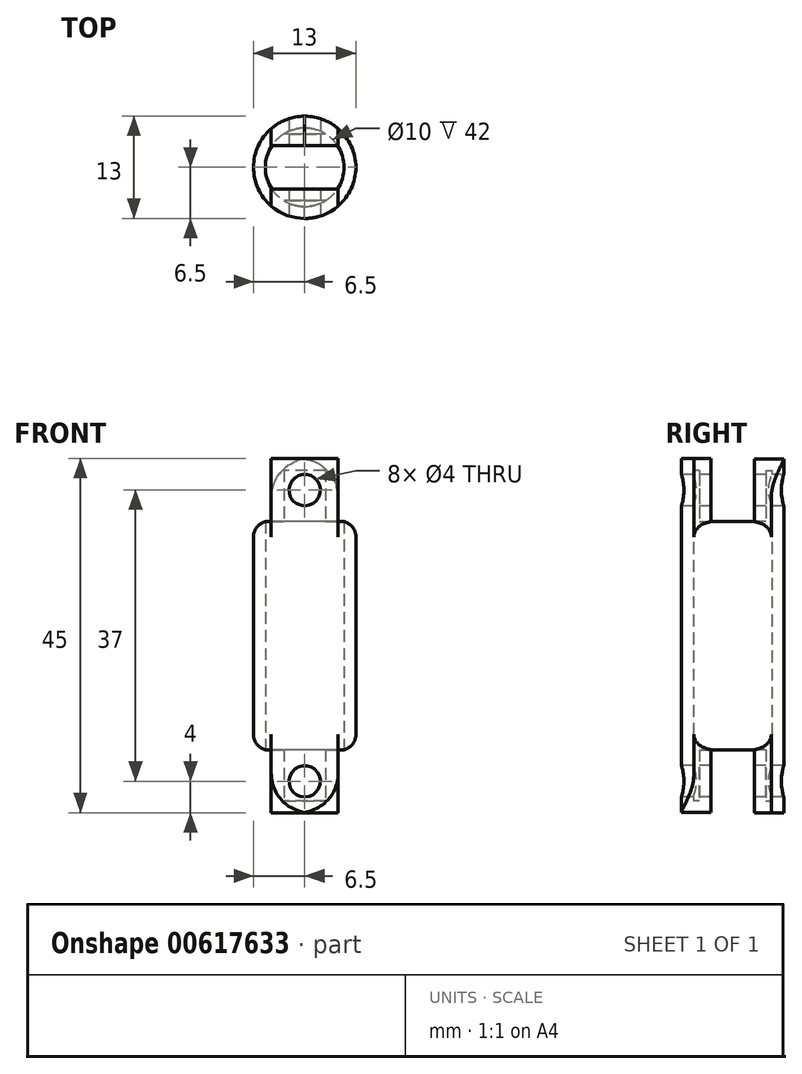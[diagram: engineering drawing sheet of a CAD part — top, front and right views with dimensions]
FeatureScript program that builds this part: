
annotation { "Feature Type Name" : "Feature", "Feature Type Description" : "" }
export const myFeature = defineFeature(function(context is Context, id is Id, definition is map)
    precondition{}
    {
        {
            var Q0;
            Q0=qCreatedBy(makeId("Top.planeOp"),FACE);
            var sketch = newSketch(context, id + "F0", { "sketchPlane" : qUnion([Q0])});
            skCircle(sketch, "E0", {"center": v(0, 0) * mm, "radius": 6.5 * mm});
            skSolve(sketch);
        }
        {
            var Q0;
            Q0 = qSketchRegion(id + "F0", true);
            extrude(context, id + "F1", {"entities" : qUnion([Q0]), "depth" : 45 * mm, "offsetDistance" : 25 * mm});
        }
        {
            var Q0;
            Q0=makeQuery(id+"F1.opExtrude","CAP_FACE",FACE,{"disambiguationData":[OSD([sQuery(id+"F0.wireOp",EDGE,"E0")])],"isStart":true});
            var sketch = newSketch(context, id + "F2", { "sketchPlane" : qUnion([Q0])});
            skLineSegment(sketch, "E1.bottom", {"start": v(6, 2.75) * mm, "end": v(-6, 2.75) * mm});
            skLineSegment(sketch, "E1.top", {"start": v(6, -2.75) * mm, "end": v(-6, -2.75) * mm});
            skLineSegment(sketch, "E1.left", {"start": v(6, 2.75) * mm, "end": v(6, -2.75) * mm});
            skLineSegment(sketch, "E1.right", {"start": v(-6, 2.75) * mm, "end": v(-6, -2.75) * mm});
            skPoint(sketch, "E1.middle", {"position": v(0, 0) * mm});
            skLineSegment(sketch, "E2.bottom", {"start": v(-4.25, 5) * mm, "end": v(-7.75, 5) * mm});
            skLineSegment(sketch, "E2.top", {"start": v(-4.25, -5) * mm, "end": v(-7.75, -5) * mm});
            skLineSegment(sketch, "E2.left", {"start": v(-4.25, 5) * mm, "end": v(-4.25, -5) * mm});
            skLineSegment(sketch, "E2.right", {"start": v(-7.75, 5) * mm, "end": v(-7.75, -5) * mm});
            skPoint(sketch, "E2.middle", {"position": v(-6, 0) * mm});
            skLineSegment(sketch, "E3.bottom", {"start": v(7.75, 5) * mm, "end": v(4.25, 5) * mm});
            skLineSegment(sketch, "E3.top", {"start": v(7.75, -5) * mm, "end": v(4.25, -5) * mm});
            skLineSegment(sketch, "E3.left", {"start": v(7.75, 5) * mm, "end": v(7.75, -5) * mm});
            skLineSegment(sketch, "E3.right", {"start": v(4.25, 5) * mm, "end": v(4.25, -5) * mm});
            skPoint(sketch, "E3.middle", {"position": v(6, 0) * mm});
            skSolve(sketch);
        }
        {
            var Q0;
            Q0 = qSketchRegion(id + "F2", true);
            extrude(context, id + "F3", {"entities" : qUnion([Q0]), "operationType" : NewBodyOperationType.REMOVE, "oppositeDirection" : true, "depth" : 8 * mm, "offsetDistance" : 25 * mm});
        }
        {
            var Q0;
            Q0=makeQuery(id+"F1.opExtrude","CAP_FACE",FACE,{"disambiguationData":[OSD([sQuery(id+"F0.wireOp",EDGE,"E0")])],"isStart":false});
            var sketch = newSketch(context, id + "F4", { "sketchPlane" : qUnion([Q0])});
            skLineSegment(sketch, "E4.bottom", {"start": v(6, 2.75) * mm, "end": v(-6, 2.75) * mm});
            skLineSegment(sketch, "E4.top", {"start": v(6, -2.75) * mm, "end": v(-6, -2.75) * mm});
            skLineSegment(sketch, "E4.left", {"start": v(6, 2.75) * mm, "end": v(6, -2.75) * mm});
            skLineSegment(sketch, "E4.right", {"start": v(-6, 2.75) * mm, "end": v(-6, -2.75) * mm});
            skPoint(sketch, "E4.middle", {"position": v(0, 0) * mm});
            skLineSegment(sketch, "E5.bottom", {"start": v(7.75, 5) * mm, "end": v(4.25, 5) * mm});
            skLineSegment(sketch, "E5.top", {"start": v(7.75, -5) * mm, "end": v(4.25, -5) * mm});
            skLineSegment(sketch, "E5.left", {"start": v(7.75, 5) * mm, "end": v(7.75, -5) * mm});
            skLineSegment(sketch, "E5.right", {"start": v(4.25, 5) * mm, "end": v(4.25, -5) * mm});
            skPoint(sketch, "E5.middle", {"position": v(6, 0) * mm});
            skLineSegment(sketch, "E6.bottom", {"start": v(-4.25, 5) * mm, "end": v(-7.75, 5) * mm});
            skLineSegment(sketch, "E6.top", {"start": v(-4.25, -5) * mm, "end": v(-7.75, -5) * mm});
            skLineSegment(sketch, "E6.left", {"start": v(-4.25, 5) * mm, "end": v(-4.25, -5) * mm});
            skLineSegment(sketch, "E6.right", {"start": v(-7.75, 5) * mm, "end": v(-7.75, -5) * mm});
            skPoint(sketch, "E6.middle", {"position": v(-6, 0) * mm});
            skSolve(sketch);
        }
        {
            var Q0;
            Q0 = qSketchRegion(id + "F4", true);
            extrude(context, id + "F5", {"entities" : qUnion([Q0]), "operationType" : NewBodyOperationType.REMOVE, "oppositeDirection" : true, "depth" : 8 * mm, "offsetDistance" : 25 * mm});
        }
        {
            var Q0;
            Q0=makeQuery(id+"F3.boolean.opBoolean","COPY",FACE,{"derivedFrom":makeQuery(id+"F3.opExtrude","SWEPT_FACE",FACE,{"disambiguationData":[OSD([sQuery(id+"F2.wireOp",EDGE,"E1.top")])]})});
            var sketch = newSketch(context, id + "F6", { "sketchPlane" : qUnion([Q0])});
            skCircle(sketch, "E7", {"center": v(0, 4) * mm, "radius": 2 * mm});
            skPoint(sketch, "E7.centerSnap0", {"position": v(-4.18, 4) * mm});
            skSolve(sketch);
        }
        {
            var Q0;
            Q0=makeQuery(id+"F3.boolean.opBoolean","COPY",FACE,{"derivedFrom":makeQuery(id+"F3.opExtrude","CAP_FACE",FACE,{"disambiguationData":[OSD([sQuery(id+"F2.wireOp",EDGE,"E1.bottom"),sQuery(id+"F2.wireOp",EDGE,"E1.top"),sQuery(id+"F2.wireOp",EDGE,"E2.bottom"),sQuery(id+"F2.wireOp",EDGE,"E2.top"),sQuery(id+"F2.wireOp",EDGE,"E2.left"),sQuery(id+"F2.wireOp",EDGE,"E2.right"),sQuery(id+"F2.wireOp",EDGE,"E3.bottom"),sQuery(id+"F2.wireOp",EDGE,"E3.top"),sQuery(id+"F2.wireOp",EDGE,"E3.left"),sQuery(id+"F2.wireOp",EDGE,"E3.right")])],"isStart":false})});
            var Q1;
            Q1=makeQuery(id+"F5.boolean.opBoolean","COPY",FACE,{"derivedFrom":makeQuery(id+"F5.opExtrude","CAP_FACE",FACE,{"disambiguationData":[OSD([sQuery(id+"F4.wireOp",EDGE,"E4.bottom"),sQuery(id+"F4.wireOp",EDGE,"E4.top"),sQuery(id+"F4.wireOp",EDGE,"E5.bottom"),sQuery(id+"F4.wireOp",EDGE,"E5.top"),sQuery(id+"F4.wireOp",EDGE,"E5.left"),sQuery(id+"F4.wireOp",EDGE,"E5.right"),sQuery(id+"F4.wireOp",EDGE,"E6.bottom"),sQuery(id+"F4.wireOp",EDGE,"E6.top"),sQuery(id+"F4.wireOp",EDGE,"E6.left"),sQuery(id+"F4.wireOp",EDGE,"E6.right")])],"isStart":false})});
            shell(context, id + "F7", {"entities" : qUnion([Q0, Q1]), "thickness" : 1.5 * mm});
        }
        {
            var Q0;
            Q0=makeQuery(id+"F5.boolean.opBoolean","COPY",FACE,{"derivedFrom":makeQuery(id+"F5.opExtrude","SWEPT_FACE",FACE,{"disambiguationData":[OSD([sQuery(id+"F4.wireOp",EDGE,"E4.bottom")])]})});
            var sketch = newSketch(context, id + "F8", { "sketchPlane" : qUnion([Q0])});
            skCircle(sketch, "E8", {"center": v(0, 41) * mm, "radius": 2 * mm});
            skPoint(sketch, "E8.centerSnap0", {"position": v(-4.25, 41) * mm});
            skPoint(sketch, "E9", {"position": v(6.83, 41) * mm});
            skSolve(sketch);
        }
        {
            var Q0;
            Q0 = qSketchRegion(id + "F8", true);
            extrude(context, id + "F9", {"entities" : qUnion([Q0]), "operationType" : NewBodyOperationType.REMOVE, "oppositeDirection" : true, "depth" : 25 * mm, "offsetDistance" : 25 * mm, "hasSecondDirection" : true, "secondDirectionOppositeDirection" : false, "secondDirectionDepth" : 25 * mm});
        }
        {
            var Q0;
            Q0 = qSketchRegion(id + "F6", true);
            extrude(context, id + "F10", {"entities" : qUnion([Q0]), "operationType" : NewBodyOperationType.REMOVE, "oppositeDirection" : true, "depth" : 25 * mm, "offsetDistance" : 25 * mm, "hasSecondDirection" : true, "secondDirectionOppositeDirection" : false, "secondDirectionDepth" : 25 * mm});
        }
        {
            var Q0;
            Q0=makeQuery(id+"F5.boolean.opBoolean","COPY",FACE,{"derivedFrom":makeQuery(id+"F5.opExtrude","SWEPT_FACE",FACE,{"disambiguationData":[OSD([sQuery(id+"F4.wireOp",EDGE,"E4.bottom")])]})});
            var sketch = newSketch(context, id + "F11", { "sketchPlane" : qUnion([Q0])});
            skCircle(sketch, "E10", {"center": v(0, 41) * mm, "radius": 5 * mm});
            skSolve(sketch);
        }
        {
            var Q0;
            Q0 = qSketchRegion(id + "F11", true);
            extrude(context, id + "F12", {"entities" : qUnion([Q0]), "operationType" : NewBodyOperationType.REMOVE, "depth" : 5.5 * mm, "offsetDistance" : 25 * mm});
        }
        {
            var Q0;
            Q0=makeQuery(id+"F3.boolean.opBoolean","COPY",FACE,{"derivedFrom":makeQuery(id+"F3.opExtrude","SWEPT_FACE",FACE,{"disambiguationData":[OSD([sQuery(id+"F2.wireOp",EDGE,"E1.top")])]})});
            var sketch = newSketch(context, id + "F13", { "sketchPlane" : qUnion([Q0])});
            skCircle(sketch, "E11", {"center": v(0, 4) * mm, "radius": 5 * mm});
            skSolve(sketch);
        }
        {
            var Q0;
            Q0 = qSketchRegion(id + "F13", true);
            extrude(context, id + "F14", {"entities" : qUnion([Q0]), "operationType" : NewBodyOperationType.REMOVE, "depth" : 5.5 * mm, "offsetDistance" : 25 * mm});
        }
        {
            var Q0;
            {var subQ0=sQuery(id+"F4.wireOp",EDGE,"E5.right");Q0=makeQuery(id+"F5.boolean.opBoolean","COPY",EDGE,{"derivedFrom":makeQuery(id+"F5.opExtrude","CAP_EDGE",EDGE,{"disambiguationData":[OSD([subQ0]),TDD([makeQuery(id+"F4.imprint","IMPRINT",EDGE,{"disambiguationData":[TD([[makeQuery(id+"F4.imprint","INTERSECT",VERTEX,{"derivedFrom":[sQuery(id+"F4.wireOp",EDGE,"E4.top"),subQ0]}),-1.0]])],"derivedFrom":subQ0}),makeQuery(id+"F4.imprint","IMPRINT",EDGE,{"disambiguationData":[TD([[makeQuery(id+"F4.imprint","INTERSECT",VERTEX,{"derivedFrom":[sQuery(id+"F4.wireOp",EDGE,"E5.top"),subQ0]}),1.0]])],"derivedFrom":subQ0})])],"isStart":true})});}
            var Q1;
            {var subQ0=sQuery(id+"F4.wireOp",EDGE,"E5.right");Q1=makeQuery(id+"F5.boolean.opBoolean","COPY",EDGE,{"derivedFrom":makeQuery(id+"F5.opExtrude","CAP_EDGE",EDGE,{"disambiguationData":[OSD([subQ0]),TDD([makeQuery(id+"F4.imprint","IMPRINT",EDGE,{"disambiguationData":[TD([[makeQuery(id+"F4.imprint","INTERSECT",VERTEX,{"derivedFrom":[sQuery(id+"F4.wireOp",EDGE,"E5.bottom"),subQ0]}),-1.0]])],"derivedFrom":subQ0}),makeQuery(id+"F4.imprint","IMPRINT",EDGE,{"disambiguationData":[TD([[makeQuery(id+"F4.imprint","INTERSECT",VERTEX,{"derivedFrom":[sQuery(id+"F4.wireOp",EDGE,"E4.bottom"),subQ0]}),1.0]])],"derivedFrom":subQ0})])],"isStart":true})});}
            var Q2;
            {var subQ0=sQuery(id+"F4.wireOp",EDGE,"E6.left");Q2=makeQuery(id+"F5.boolean.opBoolean","COPY",EDGE,{"derivedFrom":makeQuery(id+"F5.opExtrude","CAP_EDGE",EDGE,{"disambiguationData":[OSD([subQ0]),TDD([makeQuery(id+"F4.imprint","IMPRINT",EDGE,{"disambiguationData":[TD([[makeQuery(id+"F4.imprint","INTERSECT",VERTEX,{"derivedFrom":[sQuery(id+"F4.wireOp",EDGE,"E4.top"),subQ0]}),-1.0]])],"derivedFrom":subQ0}),makeQuery(id+"F4.imprint","IMPRINT",EDGE,{"disambiguationData":[TD([[makeQuery(id+"F4.imprint","INTERSECT",VERTEX,{"derivedFrom":[sQuery(id+"F4.wireOp",EDGE,"E6.top"),subQ0]}),1.0]])],"derivedFrom":subQ0})])],"isStart":true})});}
            var Q3;
            {var subQ0=sQuery(id+"F4.wireOp",EDGE,"E6.left");Q3=makeQuery(id+"F5.boolean.opBoolean","COPY",EDGE,{"derivedFrom":makeQuery(id+"F5.opExtrude","CAP_EDGE",EDGE,{"disambiguationData":[OSD([subQ0]),TDD([makeQuery(id+"F4.imprint","IMPRINT",EDGE,{"disambiguationData":[TD([[makeQuery(id+"F4.imprint","INTERSECT",VERTEX,{"derivedFrom":[sQuery(id+"F4.wireOp",EDGE,"E6.bottom"),subQ0]}),-1.0]])],"derivedFrom":subQ0}),makeQuery(id+"F4.imprint","IMPRINT",EDGE,{"disambiguationData":[TD([[makeQuery(id+"F4.imprint","INTERSECT",VERTEX,{"derivedFrom":[sQuery(id+"F4.wireOp",EDGE,"E4.bottom"),subQ0]}),1.0]])],"derivedFrom":subQ0})])],"isStart":true})});}
            var Q4;
            {var subQ0=sQuery(id+"F2.wireOp",EDGE,"E2.left");Q4=makeQuery(id+"F3.boolean.opBoolean","COPY",EDGE,{"derivedFrom":makeQuery(id+"F3.opExtrude","CAP_EDGE",EDGE,{"disambiguationData":[OSD([subQ0]),TDD([makeQuery(id+"F2.imprint","IMPRINT",EDGE,{"disambiguationData":[TD([[makeQuery(id+"F2.imprint","INTERSECT",VERTEX,{"derivedFrom":[sQuery(id+"F2.wireOp",EDGE,"E1.top"),subQ0]}),-1.0]])],"derivedFrom":subQ0}),makeQuery(id+"F2.imprint","IMPRINT",EDGE,{"disambiguationData":[TD([[makeQuery(id+"F2.imprint","INTERSECT",VERTEX,{"derivedFrom":[sQuery(id+"F2.wireOp",EDGE,"E2.top"),subQ0]}),1.0]])],"derivedFrom":subQ0})])],"isStart":true})});}
            var Q5;
            {var subQ0=sQuery(id+"F2.wireOp",EDGE,"E3.right");Q5=makeQuery(id+"F3.boolean.opBoolean","COPY",EDGE,{"derivedFrom":makeQuery(id+"F3.opExtrude","CAP_EDGE",EDGE,{"disambiguationData":[OSD([subQ0]),TDD([makeQuery(id+"F2.imprint","IMPRINT",EDGE,{"disambiguationData":[TD([[makeQuery(id+"F2.imprint","INTERSECT",VERTEX,{"derivedFrom":[sQuery(id+"F2.wireOp",EDGE,"E1.top"),subQ0]}),-1.0]])],"derivedFrom":subQ0}),makeQuery(id+"F2.imprint","IMPRINT",EDGE,{"disambiguationData":[TD([[makeQuery(id+"F2.imprint","INTERSECT",VERTEX,{"derivedFrom":[sQuery(id+"F2.wireOp",EDGE,"E3.top"),subQ0]}),1.0]])],"derivedFrom":subQ0})])],"isStart":true})});}
            var Q6;
            {var subQ0=sQuery(id+"F2.wireOp",EDGE,"E3.right");Q6=makeQuery(id+"F3.boolean.opBoolean","COPY",EDGE,{"derivedFrom":makeQuery(id+"F3.opExtrude","CAP_EDGE",EDGE,{"disambiguationData":[OSD([subQ0]),TDD([makeQuery(id+"F2.imprint","IMPRINT",EDGE,{"disambiguationData":[TD([[makeQuery(id+"F2.imprint","INTERSECT",VERTEX,{"derivedFrom":[sQuery(id+"F2.wireOp",EDGE,"E3.bottom"),subQ0]}),-1.0]])],"derivedFrom":subQ0}),makeQuery(id+"F2.imprint","IMPRINT",EDGE,{"disambiguationData":[TD([[makeQuery(id+"F2.imprint","INTERSECT",VERTEX,{"derivedFrom":[sQuery(id+"F2.wireOp",EDGE,"E1.bottom"),subQ0]}),1.0]])],"derivedFrom":subQ0})])],"isStart":true})});}
            var Q7;
            {var subQ0=sQuery(id+"F2.wireOp",EDGE,"E2.left");Q7=makeQuery(id+"F3.boolean.opBoolean","COPY",EDGE,{"derivedFrom":makeQuery(id+"F3.opExtrude","CAP_EDGE",EDGE,{"disambiguationData":[OSD([subQ0]),TDD([makeQuery(id+"F2.imprint","IMPRINT",EDGE,{"disambiguationData":[TD([[makeQuery(id+"F2.imprint","INTERSECT",VERTEX,{"derivedFrom":[sQuery(id+"F2.wireOp",EDGE,"E2.bottom"),subQ0]}),-1.0]])],"derivedFrom":subQ0}),makeQuery(id+"F2.imprint","IMPRINT",EDGE,{"disambiguationData":[TD([[makeQuery(id+"F2.imprint","INTERSECT",VERTEX,{"derivedFrom":[sQuery(id+"F2.wireOp",EDGE,"E1.bottom"),subQ0]}),1.0]])],"derivedFrom":subQ0})])],"isStart":true})});}
            fillet(context, id + "F15", {"entities" : qUnion([Q0, Q1, Q2, Q3, Q4, Q5, Q6, Q7]), "radius" : 5 * mm, "tangentPropagation" : true, "allowEdgeOverflow" : false});
        }
        {
            var Q0;
            Q0=makeQuery(id+"F5.boolean.opBoolean","INTERSECT",EDGE,{"disambiguationData":[OD(0.0)],"derivedFrom":[makeQuery(id+"F1.opExtrude","SWEPT_FACE",FACE,{"disambiguationData":[OSD([sQuery(id+"F0.wireOp",EDGE,"E0")])]}),makeQuery(id+"F5.opExtrude","CAP_FACE",FACE,{"disambiguationData":[OSD([sQuery(id+"F4.wireOp",EDGE,"E4.bottom"),sQuery(id+"F4.wireOp",EDGE,"E4.top"),sQuery(id+"F4.wireOp",EDGE,"E5.bottom"),sQuery(id+"F4.wireOp",EDGE,"E5.top"),sQuery(id+"F4.wireOp",EDGE,"E5.left"),sQuery(id+"F4.wireOp",EDGE,"E5.right"),sQuery(id+"F4.wireOp",EDGE,"E6.bottom"),sQuery(id+"F4.wireOp",EDGE,"E6.top"),sQuery(id+"F4.wireOp",EDGE,"E6.left"),sQuery(id+"F4.wireOp",EDGE,"E6.right")])],"isStart":false})]});
            var Q1;
            Q1=makeQuery(id+"F3.boolean.opBoolean","INTERSECT",EDGE,{"disambiguationData":[OD(1.0)],"derivedFrom":[makeQuery(id+"F1.opExtrude","SWEPT_FACE",FACE,{"disambiguationData":[OSD([sQuery(id+"F0.wireOp",EDGE,"E0")])]}),makeQuery(id+"F3.opExtrude","CAP_FACE",FACE,{"disambiguationData":[OSD([sQuery(id+"F2.wireOp",EDGE,"E1.bottom"),sQuery(id+"F2.wireOp",EDGE,"E1.top"),sQuery(id+"F2.wireOp",EDGE,"E2.bottom"),sQuery(id+"F2.wireOp",EDGE,"E2.top"),sQuery(id+"F2.wireOp",EDGE,"E2.left"),sQuery(id+"F2.wireOp",EDGE,"E2.right"),sQuery(id+"F2.wireOp",EDGE,"E3.bottom"),sQuery(id+"F2.wireOp",EDGE,"E3.top"),sQuery(id+"F2.wireOp",EDGE,"E3.left"),sQuery(id+"F2.wireOp",EDGE,"E3.right")])],"isStart":false})]});
            fillet(context, id + "F16", {"entities" : qUnion([Q0, Q1]), "radius" : 2 * mm, "tangentPropagation" : true, "allowEdgeOverflow" : false});
        }
    });
